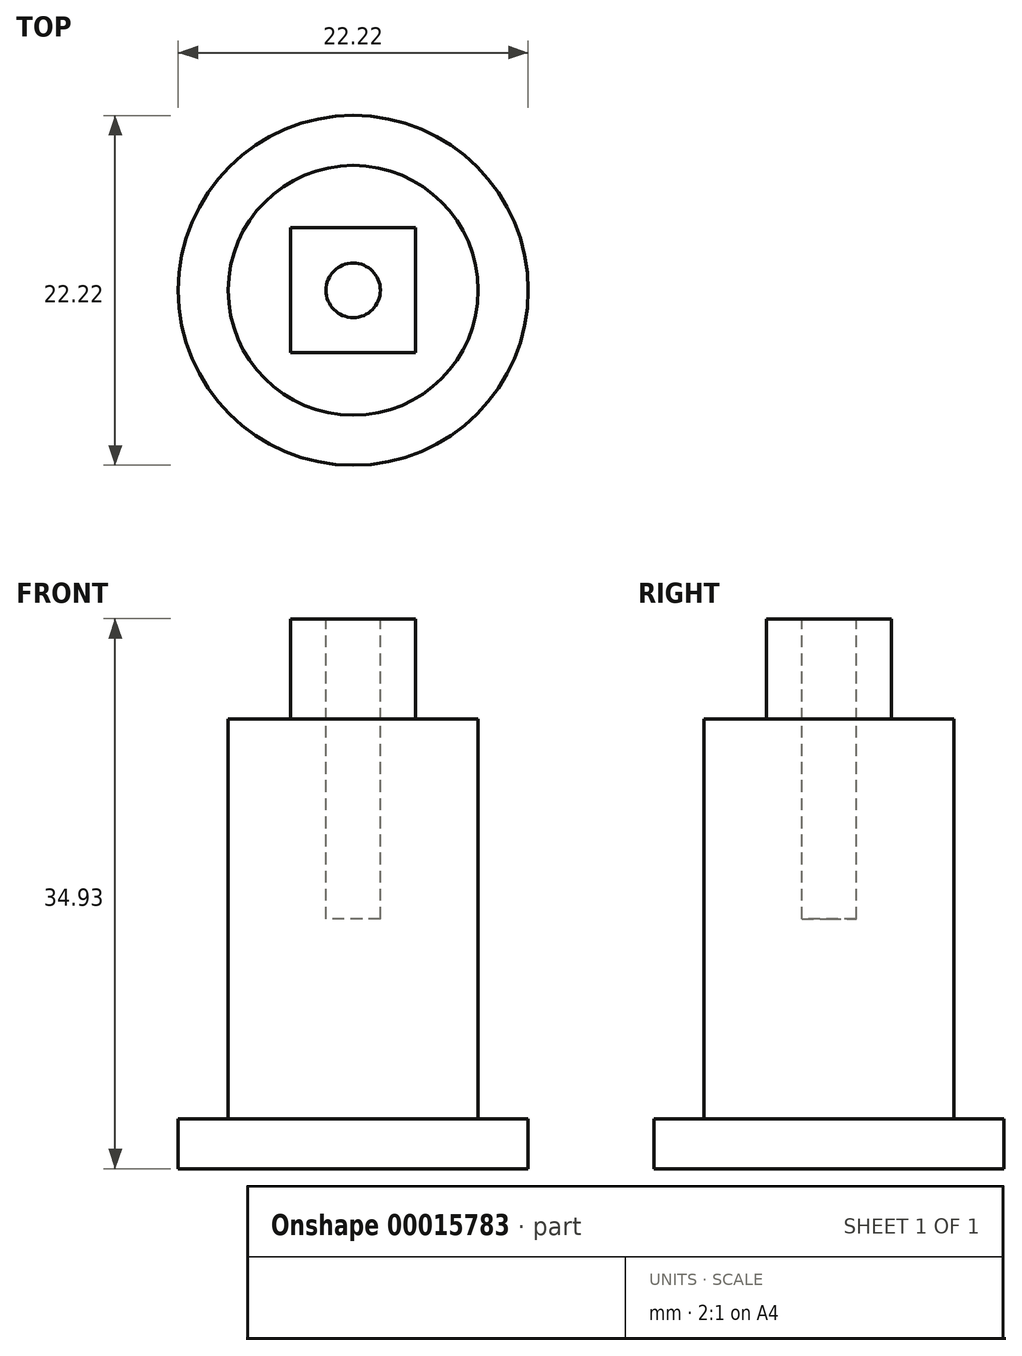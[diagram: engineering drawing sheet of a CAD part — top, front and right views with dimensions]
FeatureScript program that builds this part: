
annotation { "Feature Type Name" : "Feature", "Feature Type Description" : "" }
export const myFeature = defineFeature(function(context is Context, id is Id, definition is map)
    precondition{}
    {
        {
            var Q0;
            Q0=qCreatedBy(makeId("Top.planeOp"),FACE);
            var sketch = newSketch(context, id + "F0", { "sketchPlane" : qUnion([Q0])});
            skCircle(sketch, "E0", {"center": v(0, 0) * mm, "radius": 11.11 * mm});
            skSolve(sketch);
        }
        {
            var Q0;
            Q0 = qSketchRegion(id + "F0", true);
            extrude(context, id + "F1", {"entities" : qUnion([Q0]), "depth" : 3.17 * mm});
        }
        {
            var Q0;
            Q0=makeQuery(id+"F1.opExtrude","CAP_FACE",FACE,{"disambiguationData":[OSD([sQuery(id+"F0.wireOp",EDGE,"E0")])],"isStart":false});
            var sketch = newSketch(context, id + "F2", { "sketchPlane" : qUnion([Q0])});
            skCircle(sketch, "E1", {"center": v(0, 0) * mm, "radius": 7.94 * mm});
            skSolve(sketch);
        }
        {
            var Q0;
            Q0 = qSketchRegion(id + "F2", true);
            extrude(context, id + "F3", {"entities" : qUnion([Q0]), "operationType" : NewBodyOperationType.ADD, "depth" : 25.4 * mm});
        }
        {
            var Q0;
            Q0=makeQuery(id+"F3.opExtrude","CAP_FACE",FACE,{"disambiguationData":[OSD([sQuery(id+"F2.wireOp",EDGE,"E1")])],"isStart":false});
            var sketch = newSketch(context, id + "F4", { "sketchPlane" : qUnion([Q0])});
            skLineSegment(sketch, "E2.bottom", {"start": v(3.97, 3.97) * mm, "end": v(-3.97, 3.97) * mm});
            skLineSegment(sketch, "E2.top", {"start": v(3.97, -3.97) * mm, "end": v(-3.97, -3.97) * mm});
            skLineSegment(sketch, "E2.left", {"start": v(3.97, 3.97) * mm, "end": v(3.97, -3.97) * mm});
            skLineSegment(sketch, "E2.right", {"start": v(-3.97, 3.97) * mm, "end": v(-3.97, -3.97) * mm});
            skPoint(sketch, "E2.middle", {"position": v(0, 0) * mm});
            skSolve(sketch);
        }
        {
            var Q0;
            Q0 = qSketchRegion(id + "F4", true);
            extrude(context, id + "F5", {"entities" : qUnion([Q0]), "operationType" : NewBodyOperationType.ADD, "depth" : 6.35 * mm});
        }
        {
            var Q0;
            Q0=makeQuery(id+"F5.opExtrude","CAP_FACE",FACE,{"disambiguationData":[OSD([sQuery(id+"F4.wireOp",EDGE,"E2.bottom"),sQuery(id+"F4.wireOp",EDGE,"E2.top"),sQuery(id+"F4.wireOp",EDGE,"E2.left"),sQuery(id+"F4.wireOp",EDGE,"E2.right")])],"isStart":false});
            var sketch = newSketch(context, id + "F6", { "sketchPlane" : qUnion([Q0])});
            skCircle(sketch, "E3", {"center": v(0, 0) * mm, "radius": 1.73 * mm});
            skSolve(sketch);
        }
        {
            var Q0;
            Q0 = qSketchRegion(id + "F6", true);
            extrude(context, id + "F7", {"entities" : qUnion([Q0]), "operationType" : NewBodyOperationType.REMOVE, "oppositeDirection" : true, "depth" : 19.05 * mm});
        }
    });
